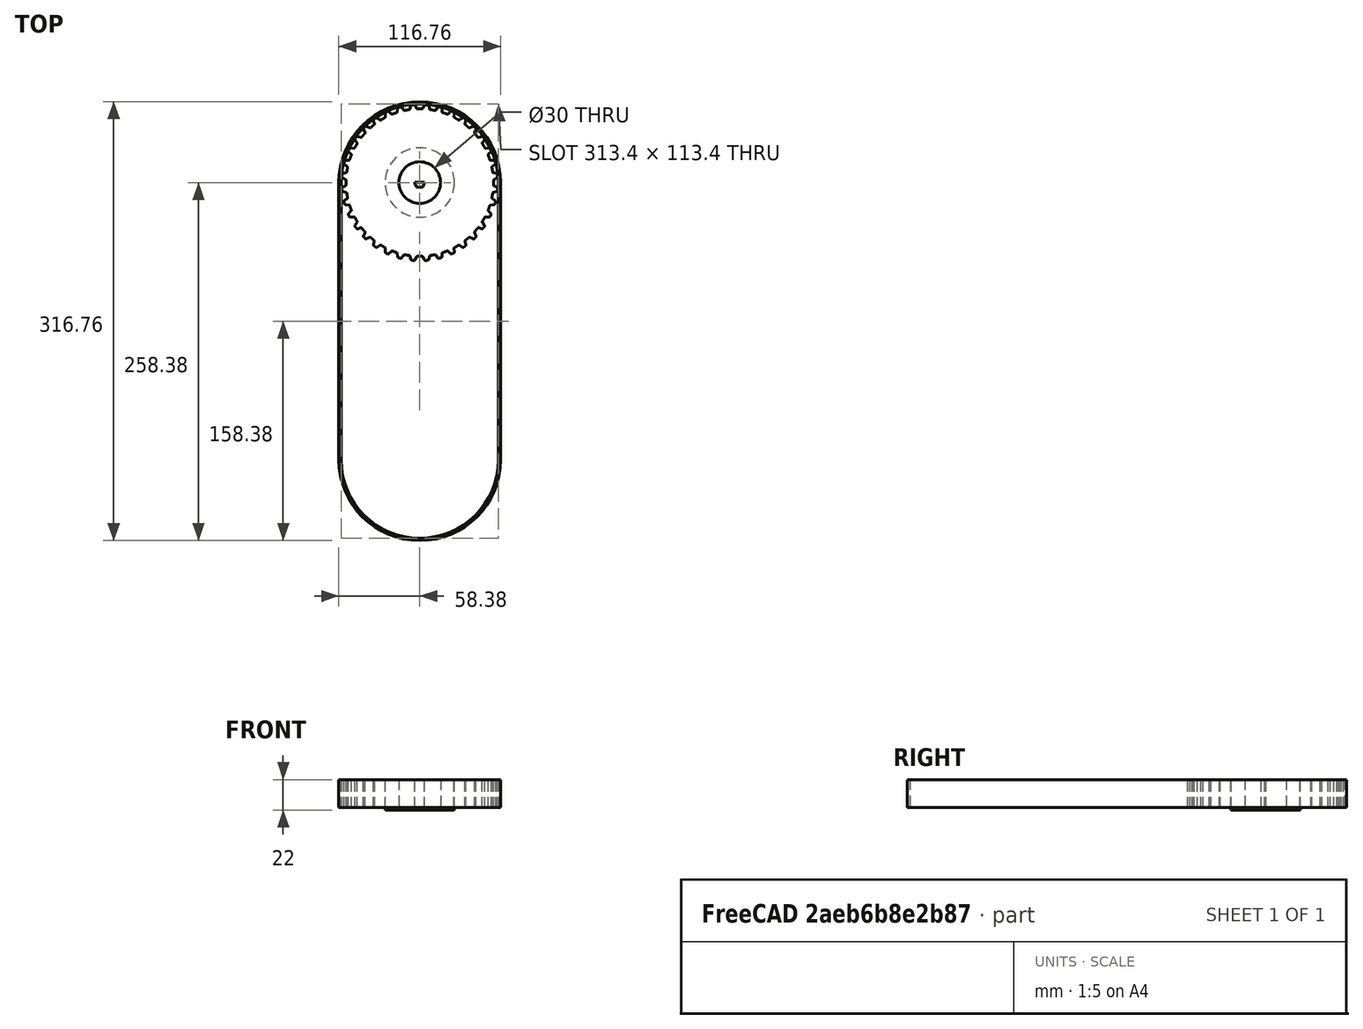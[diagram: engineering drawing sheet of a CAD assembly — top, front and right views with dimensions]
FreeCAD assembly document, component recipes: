
FREECAD ASSEMBLY — COMPONENT RECIPES ("timingBelt_project")

This assembly document has 4 components, labeled P0..P3 below (a component is one placed body or linked part). 3 of them carry a construction recipe — the FreeCAD feature program that regenerates the part from scratch, quoted from this document or its linked companion documents; the rest are supplied as boundary geometry only. No exploded tour is included for this assembly.
COMPONENT P0 — geometry summary ("Assembly"; no construction recipe available for this part):
  bounding box: 312.7 x 116.8 x 22.0 mm
  tessellated surface: 7,616 triangles
  volume: 2804284323271667013111902858605543948822203563141897321232698220236942979653550783689765873638178816 mm^3 (349181032514096101288077122776061614341965794242516699144909802003678554595383843347290784792576% of its bounding box)
  symmetry: 2-fold rotationally symmetric about the z axis
COMPONENT P1 — recipe-attached ("belt", modeled in this document).
Construction recipe (the document's own serialized feature program — sketch geometry with constraints, then the solid features built on it; lengths are millimeters unless a unit is written):

FEATURE [PartDesign::CoordinateSystem] LCS_Origin004
  AttacherType = Attacher::AttachEngine3D
  AttachmentSupport = -> [X_Axis003]
  MapMode = 2
FEATURE [Sketcher::SketchObject] belt_sk  label="belt-sk"
  ArcFitTolerance = 1e-06
  AttachmentSupport = -> [LCS_Origin004]
  FullyConstrained = true
  MakeInternals = false
  MapMode = 5
  sketch-geometry (8):
    g0: ArcOfCircle CenterX=0 CenterY=0 CenterZ=0 NormalX=0 NormalY=0 NormalZ=1 AngleXU=0 Radius=56.7 StartAngle=1e-16 EndAngle=3.14159
    g1: ArcOfCircle CenterX=-2.7e-15 CenterY=-200 CenterZ=0 NormalX=0 NormalY=0 NormalZ=1 AngleXU=0 Radius=56.7 StartAngle=3.14159 EndAngle=6.28319
    g2: LineSegment StartX=56.7 StartY=6.9e-15 StartZ=0 EndX=56.7 EndY=-200 EndZ=0
    g3: LineSegment StartX=-56.7 StartY=6.9e-15 StartZ=0 EndX=-56.7 EndY=-200 EndZ=0
    g4: ArcOfCircle CenterX=0 CenterY=0 CenterZ=0 NormalX=0 NormalY=0 NormalZ=1 AngleXU=0 Radius=58.376 StartAngle=1e-16 EndAngle=3.14159
    g5: ArcOfCircle CenterX=-2.7e-15 CenterY=-200 CenterZ=0 NormalX=0 NormalY=0 NormalZ=1 AngleXU=0 Radius=58.376 StartAngle=3.14159 EndAngle=6.28319
    g6: LineSegment StartX=58.376 StartY=7.1e-15 StartZ=0 EndX=58.376 EndY=-200 EndZ=0
    g7: LineSegment StartX=-58.376 StartY=7.1e-15 StartZ=0 EndX=-58.376 EndY=-200 EndZ=0
  constraints (18):
    c: Tangent(g0,g2) = 1.5708
    c: Tangent(g0,g3) = -1.5708
    c: Tangent(g1,g2) = 1.5708
    c: Tangent(g1,g3) = -1.5708
    c: Equal(g0,g1)
    c: Vertical(g3)
    c: Coincident(g0,g-1)
    c: Diameter(g0) = 113.4
    c: DistanceY(g2,g2) = 200
    c: Tangent(g4,g6) = 1.5708
    c: Tangent(g4,g7) = -1.5708
    c: Tangent(g5,g6) = 1.5708
    c: Tangent(g5,g7) = -1.5708
    c: Equal(g4,g5)
    c: Vertical(g7)
    c: Coincident(g4,g0)
    c: Diameter(g4) = 116.752
    c: DistanceY(g6,g6) = 200
FEATURE [PartDesign::Pad] Pad003
  Direction = (0,0,1)
  Length = 20
  Length2 = 10
  Midplane = true
  Profile = -> belt_sk
  ReferenceAxis = -> belt_sk [N_Axis]
  Refine = true
  Suppressed = false
  Type = 0
FEATURE [PartDesign::Body] belt
  AllowCompound = false
  Group = -> [LCS_Origin004,belt_sk,Pad003]
  Origin = -> Origin003
  Tip = -> Pad003
COMPONENT P2 — recipe-attached ("pulley", modeled in this document).
Construction recipe (the document's own serialized feature program — sketch geometry with constraints, then the solid features built on it; lengths are millimeters unless a unit is written):

FEATURE [PartDesign::CoordinateSystem] LCS_Origin001
  AttacherType = Attacher::AttachEngine3D
  AttachmentSupport = -> [X_Axis001]
  MapMode = 2
FEATURE [Sketcher::SketchObject] pulley_sk
  ArcFitTolerance = 0
  AttachmentSupport = -> [LCS_Origin001]
  FullyConstrained = true
  MakeInternals = false
  MapMode = 5
  sketch-geometry (2):
    g0: Circle CenterX=0 CenterY=0 CenterZ=0 NormalX=0 NormalY=0 NormalZ=1 AngleXU=0 Radius=15
    g1: Circle CenterX=0 CenterY=0 CenterZ=0 NormalX=0 NormalY=0 NormalZ=1 AngleXU=0 Radius=56.375
  constraints (4):
    c: Coincident(g0,g-1)
    c: Diameter(g0) = 30
    c: Coincident(g1,g0)
    c: Diameter(g1) = 112.75
FEATURE [PartDesign::Pad] Pad
  Direction = (0,0,1)
  Length = 20
  Length2 = 10
  Midplane = true
  Profile = -> pulley_sk
  ReferenceAxis = -> pulley_sk [N_Axis]
  Refine = true
  Suppressed = false
  Type = 0
FEATURE [Sketcher::SketchObject] Sketch
  ArcFitTolerance = 0
  AttachmentSupport = -> [XY_Plane001]
  ExternalGeometry = -> [Pad]
  FullyConstrained = false
  MakeInternals = false
  MapMode = 5
  sketch-geometry (15):
    g0: Circle [constr] CenterX=0 CenterY=0 CenterZ=0 NormalX=0 NormalY=0 NormalZ=1 AngleXU=0 Radius=53.175
    g1: ArcOfCircle CenterX=0 CenterY=0 CenterZ=0 NormalX=0 NormalY=0 NormalZ=1 AngleXU=0 Radius=53.175 StartAngle=1.53882 EndAngle=1.60277
    g2: ArcOfCircle CenterX=0 CenterY=0 CenterZ=0 NormalX=0 NormalY=0 NormalZ=1 AngleXU=0 Radius=56.375 StartAngle=1.47308 EndAngle=1.49791
    g3: LineSegment [constr] StartX=3.63683 StartY=56.4402 StartZ=0 EndX=0 EndY=48.641 EndZ=0
    g4: LineSegment [constr] StartX=-3.55413 StartY=56.2629 StartZ=0 EndX=0 EndY=48.641 EndZ=0
    g5: ArcOfCircle CenterX=0 CenterY=0 CenterZ=0 NormalX=0 NormalY=0 NormalZ=1 AngleXU=0 Radius=56.375 StartAngle=1.64369 EndAngle=1.66851
    g6: LineSegment StartX=3.32222 StartY=55.7655 StartZ=0 EndX=2.26297 EndY=53.4939 EndZ=0
    g7: LineSegment StartX=-3.32222 StartY=55.7655 StartZ=0 EndX=-2.26297 EndY=53.4939 EndZ=0
    g8: ArcOfCircle CenterX=-1.71918 CenterY=53.7475 CenterZ=0 NormalX=0 NormalY=0 NormalZ=1 AngleXU=0 Radius=0.6 StartAngle=3.57792 EndAngle=4.74436
    g9: ArcOfCircle CenterX=1.71918 CenterY=53.7475 CenterZ=0 NormalX=0 NormalY=0 NormalZ=1 AngleXU=0 Radius=0.6 StartAngle=4.68041 EndAngle=5.84685
    g10: LineSegment StartX=-5.5 StartY=56.1061 StartZ=0 EndX=-5.5 EndY=58.1061 EndZ=0
    g11: LineSegment StartX=-5.5 StartY=58.1061 StartZ=0 EndX=5.5 EndY=58.1061 EndZ=0
    g12: LineSegment StartX=5.5 StartY=58.1061 StartZ=0 EndX=5.5 EndY=56.1061 EndZ=0
    g13: ArcOfCircle CenterX=4.04727 CenterY=55.4274 CenterZ=0 NormalX=0 NormalY=0 NormalZ=1 AngleXU=0 Radius=0.8 StartAngle=1.49791 EndAngle=2.70526
    g14: ArcOfCircle CenterX=-4.04727 CenterY=55.4274 CenterZ=0 NormalX=0 NormalY=0 NormalZ=1 AngleXU=0 Radius=0.8 StartAngle=0.436332 EndAngle=1.64369
  constraints (39):
    c: Diameter(g0) = 106.35
    c: Coincident(g0,g-1)
    c: Coincident(g1,g0)
    c: Coincident(g2,g0)
    c: PointOnObject(g5,g-3)
    c: PointOnObject(g3,g-2)
    c: PointOnObject(g4,g5)
    c: Coincident(g4,g3)
    c: Equal(g2,g5)
    c: Coincident(g2,g5)
    c: Angle(g-2,g3) = 2.70526
    c: Angle(g4,g-2) = 2.70526
    c: Parallel(g6,g3)
    c: Parallel(g7,g4)
    c: Tangent(g7,g8) = -1.5708
    c: Tangent(g1,g8) = 1.5708
    c: Tangent(g1,g9) = 1.5708
    c: Tangent(g6,g9) = 1.5708
    c: Radius(g8) = 0.6
    c: Radius(g9) = 0.6
    c: PointOnObject(g1,g0)
    c: DistanceX(g1,g1) = 3.4
    c: Coincident(g5,g10)
    c: Coincident(g10,g11)
    c: Coincident(g11,g12)
    c: Coincident(g12,g2)
    c: Vertical(g12)
    c: Vertical(g10)
    c: Symmetric(g10,g11,g-2)
    c: DistanceX(g11,g11) = 11
    c: DistanceY(g12,g12) = 2
    c: Tangent(g2,g13) = -1.5708
    c: Tangent(g6,g13) = -1.5708
    c: Radius(g13) = 0.8
    c: PointOnObject(g6,g3)
    c: Tangent(g5,g14) = -1.5708
    c: Tangent(g7,g14) = 1.5708
    c: Radius(g14) = 0.8
    c: PointOnObject(g7,g4)
FEATURE [PartDesign::Pocket] Pocket
  BaseFeature = -> Pad
  Direction = (0,0,-1)
  Length = 5
  Length2 = 5
  Midplane = true
  Profile = -> Sketch
  ReferenceAxis = -> Sketch [N_Axis]
  Refine = true
  Suppressed = false
  Type = 1
FEATURE [PartDesign::PolarPattern] PolarPattern
  Angle = 360
  Axis = -> Sketch [N_Axis]
  BaseFeature = -> Pocket
  Mode = 0
  Occurrences = 36
  Offset = 120
  Originals = -> [Pocket]
  Refine = true
  Suppressed = false
  TransformMode = 0
FEATURE [Sketcher::SketchObject] Sketch001
  ArcFitTolerance = 1e-06
  AttachmentSupport = -> [PolarPattern]
  ExternalGeometry = -> [PolarPattern]
  FullyConstrained = true
  MakeInternals = false
  MapMode = 5
  Placement = pos=(0,0,-10) rot=(1,0,0;3.14159rad)
  sketch-geometry (2):
    g0: Circle CenterX=0 CenterY=0 CenterZ=0 NormalX=0 NormalY=0 NormalZ=1 AngleXU=0 Radius=25
    g1: Circle CenterX=0 CenterY=0 CenterZ=0 NormalX=0 NormalY=0 NormalZ=1 AngleXU=0 Radius=15
  constraints (4):
    c: Coincident(g0,g-1)
    c: Diameter(g0) = 50
    c: Coincident(g1,g0)
    c: Equal(g1,g-3)
FEATURE [PartDesign::Pad] Pad001
  BaseFeature = -> PolarPattern
  Direction = (0,0,-1)
  Length = 2
  Length2 = 10
  Profile = -> Sketch001
  ReferenceAxis = -> Sketch001 [N_Axis]
  Refine = true
  Suppressed = false
  Type = 0
FEATURE [PartDesign::CoordinateSystem] p_lcs  label="p-lcs"
  AttacherType = Attacher::AttachEngine3D
  AttachmentOffset = pos=(0,0,-12) rot=(0,0,1;-13.2296rad)
  AttachmentSupport = -> [Pad001]
  MapMode = 11
  Placement = pos=(0,0,0) rot=(-0.898794,0.438371,0;3.14159rad)
  expr: .AttachmentOffset.Rotation.Angle = -Variables.angle
FEATURE [PartDesign::Body] pulley
  AllowCompound = false
  Group = -> [LCS_Origin001,pulley_sk,Pad,Sketch,Pocket,PolarPattern,Sketch001,Pad001,p_lcs]
  Origin = -> Origin001
  Tip = -> Pad001
COMPONENT P3 — recipe-attached ("tooth", modeled in this document).
Construction recipe (the document's own serialized feature program — sketch geometry with constraints, then the solid features built on it; lengths are millimeters unless a unit is written):

FEATURE [PartDesign::CoordinateSystem] LCS_Origin002
  AttacherType = Attacher::AttachEngine3D
  AttachmentSupport = -> [X_Axis002]
  MapMode = 2
FEATURE [Sketcher::SketchObject] tooth_sk  label="tooth-sk"
  ArcFitTolerance = 1e-06
  AttachmentSupport = -> [LCS_Origin002]
  FullyConstrained = true
  MakeInternals = false
  MapMode = 5
  sketch-geometry (16):
    g0: LineSegment StartX=-3.5 StartY=0.2 StartZ=0 EndX=-3.5 EndY=-0.8 EndZ=0
    g1: LineSegment StartX=-3.5 StartY=-0.8 StartZ=0 EndX=-3.36013 EndY=-0.8 EndZ=0
    g2: LineSegment StartX=-3.17219 StartY=-0.931596 StartZ=0 EndX=-2.50175 EndY=-2.77362 EndZ=0
    g3: LineSegment StartX=-1.75 StartY=-3.3 StartZ=0 EndX=1.75 EndY=-3.3 EndZ=0
    g4: LineSegment StartX=2.50175 StartY=-2.77362 StartZ=0 EndX=3.17219 EndY=-0.931596 EndZ=0
    g5: LineSegment StartX=3.36013 StartY=-0.8 StartZ=0 EndX=3.5 EndY=-0.8 EndZ=0
    g6: LineSegment StartX=3.5 StartY=-0.8 StartZ=0 EndX=3.5 EndY=0.2 EndZ=0
    g7: LineSegment StartX=3.5 StartY=0.2 StartZ=0 EndX=-3.5 EndY=0.2 EndZ=0
    g8: ArcOfCircle CenterX=-1.75 CenterY=-2.5 CenterZ=0 NormalX=0 NormalY=0 NormalZ=1 AngleXU=0 Radius=0.8 StartAngle=3.49066 EndAngle=4.71239
    g9: GeomPoint [constr] X=-2.31017 Y=-3.3 Z=0
    g10: ArcOfCircle CenterX=1.75 CenterY=-2.5 CenterZ=0 NormalX=0 NormalY=0 NormalZ=1 AngleXU=0 Radius=0.8 StartAngle=4.71239 EndAngle=5.93412
    g11: GeomPoint [constr] X=2.31017 Y=-3.3 Z=0
    g12: ArcOfCircle CenterX=-3.36013 CenterY=-1 CenterZ=0 NormalX=0 NormalY=0 NormalZ=1 AngleXU=0 Radius=0.2 StartAngle=0.349066 EndAngle=1.5708
    g13: GeomPoint [constr] X=-3.22009 Y=-0.8 Z=0
    g14: ArcOfCircle CenterX=3.36013 CenterY=-1 CenterZ=0 NormalX=0 NormalY=0 NormalZ=1 AngleXU=0 Radius=0.2 StartAngle=1.5708 EndAngle=2.79253
    g15: GeomPoint [constr] X=3.22009 Y=-0.8 Z=0
  constraints (38):
    c: Vertical(g0)
    c: Coincident(g0,g1)
    c: Horizontal(g1)
    c: Horizontal(g5)
    c: Coincident(g5,g6)
    c: Vertical(g6)
    c: Coincident(g6,g7)
    c: Coincident(g7,g0)
    c: DistanceX(g7,g7) = 7
    c: DistanceY(g6,g6) = 1
    c: DistanceY(g-1,g6) = 0.2
    c: Symmetric(g0,g6,g-2)
    c: PointOnObject(g9,g2)
    c: PointOnObject(g9,g3)
    c: Tangent(g2,g8) = -1.5708
    c: Tangent(g3,g8) = -1.5708
    c: PointOnObject(g11,g3)
    c: PointOnObject(g11,g4)
    c: Tangent(g3,g10) = -1.5708
    c: Tangent(g4,g10) = -1.5708
    c: Radius(g10) = 0.8
    c: DistanceX(g3,g3) = 3.5
    c: Equal(g8,g10)
    c: Angle(g4,g-2) = 0.349066
    c: Angle(g-2,g2) = 0.349066
    c: Horizontal(g5,g0)
    c: DistanceY(g3,g6) = 3.5
    c: Symmetric(g3,g3,g-2)
    c: PointOnObject(g13,g1)
    c: PointOnObject(g13,g2)
    c: Tangent(g1,g12) = 1.5708
    c: Tangent(g2,g12) = 1.5708
    c: Radius(g12) = 0.2
    c: PointOnObject(g15,g5)
    c: PointOnObject(g15,g4)
    c: Tangent(g5,g14) = 1.5708
    c: Tangent(g4,g14) = 1.5708
    c: Radius(g14) = 0.2
FEATURE [PartDesign::Pad] Pad002
  Direction = (0,0,1)
  Length = 20
  Length2 = 10
  Midplane = true
  Profile = -> tooth_sk
  ReferenceAxis = -> tooth_sk [N_Axis]
  Refine = true
  Suppressed = false
  Type = 0
FEATURE [PartDesign::CoordinateSystem] LCS_Origin003  label="tooth-LCS"
  AttacherType = Attacher::AttachEngine3D
  AttachmentSupport = -> [X_Axis002]
  MapMode = 2
FEATURE [PartDesign::Body] tooth
  AllowCompound = false
  Group = -> [LCS_Origin002,tooth_sk,Pad002,LCS_Origin003]
  Origin = -> Origin002
  Tip = -> Pad002
PROVENANCE & LICENSES
A FreeCAD (.FCStd) document from a public repository crawl; recipes are the document's own serialized feature recipes (and, for linked parts, companion documents' recipes).
License: as declared in the source repository (recorded in the dataset sidecar).
